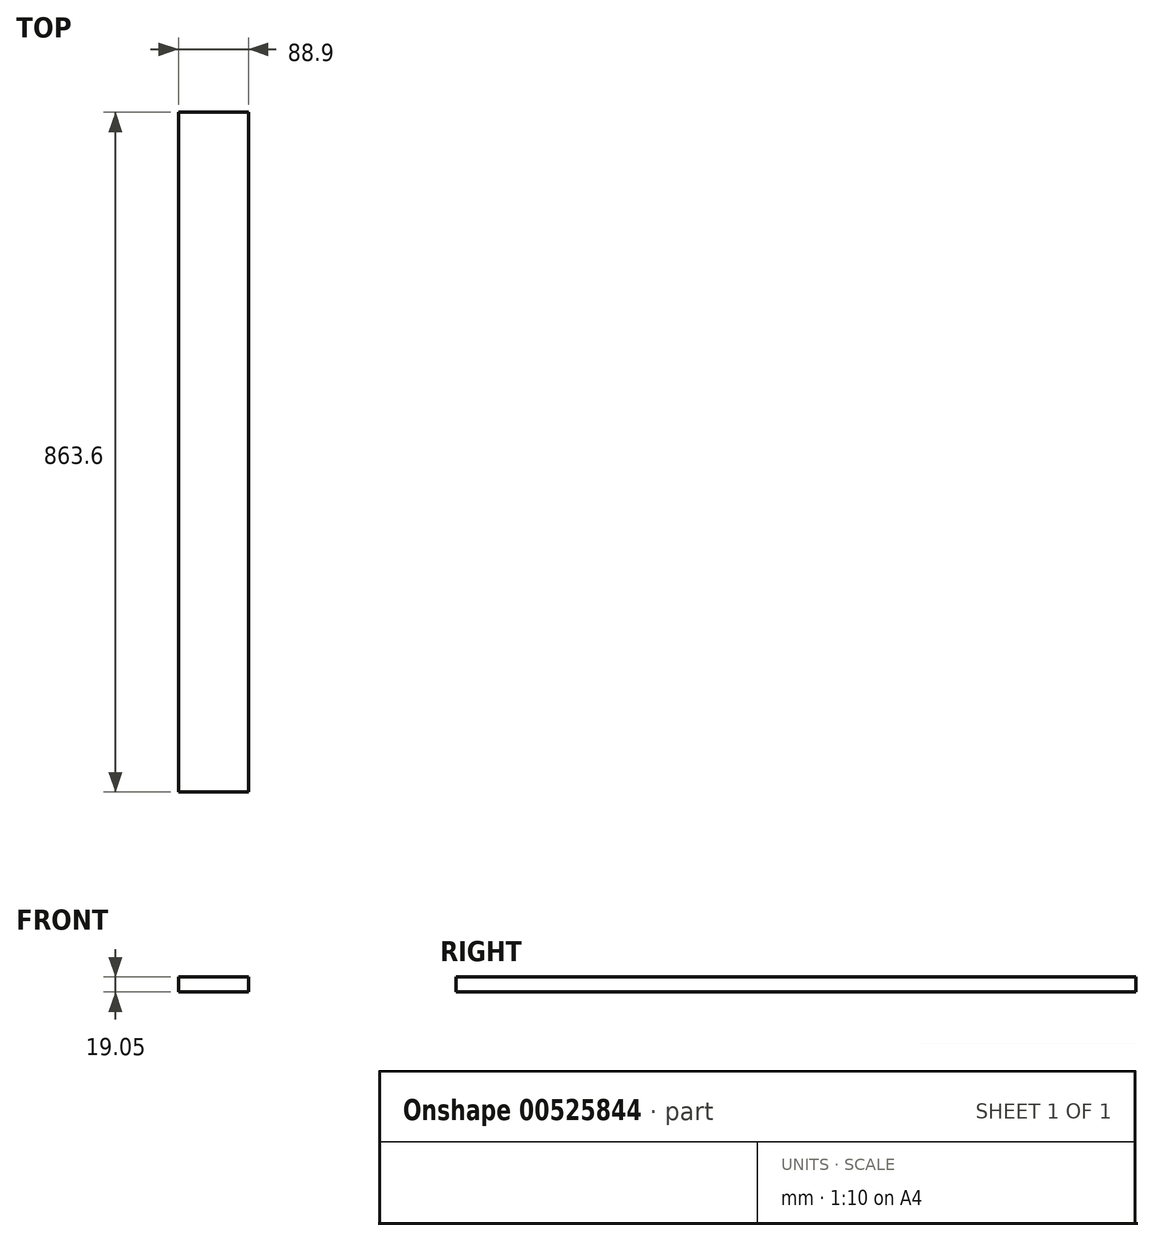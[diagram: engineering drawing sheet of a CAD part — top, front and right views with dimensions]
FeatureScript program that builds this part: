
annotation { "Feature Type Name" : "Feature", "Feature Type Description" : "" }
export const myFeature = defineFeature(function(context is Context, id is Id, definition is map)
    precondition{}
    {
        {
            var Q0;
            Q0=qCreatedBy(makeId("Front.planeOp"),FACE);
            var sketch = newSketch(context, id + "F0", { "sketchPlane" : qUnion([Q0])});
            skLineSegment(sketch, "E0.bottom", {"start": v(0, 0) * mm, "end": v(88.9, 0) * mm});
            skLineSegment(sketch, "E0.top", {"start": v(0, 19.05) * mm, "end": v(88.9, 19.05) * mm});
            skLineSegment(sketch, "E0.left", {"start": v(0, 0) * mm, "end": v(0, 19.05) * mm});
            skLineSegment(sketch, "E0.right", {"start": v(88.9, 0) * mm, "end": v(88.9, 19.05) * mm});
            skSolve(sketch);
        }
        {
            var Q0;
            Q0=makeQuery(id+"F0.imprint","IMPRINT",FACE,{"disambiguationData":[TD([[makeQuery(id+"F0.imprint","IMPRINT",EDGE,{"derivedFrom":sQuery(id+"F0.wireOp",EDGE,"E0.bottom")}),1.0]])]});
            extrude(context, id + "F1", {"entities" : qUnion([Q0]), "depth" : 863.6 * mm, "offsetDistance" : 25.4 * mm});
        }
    });
